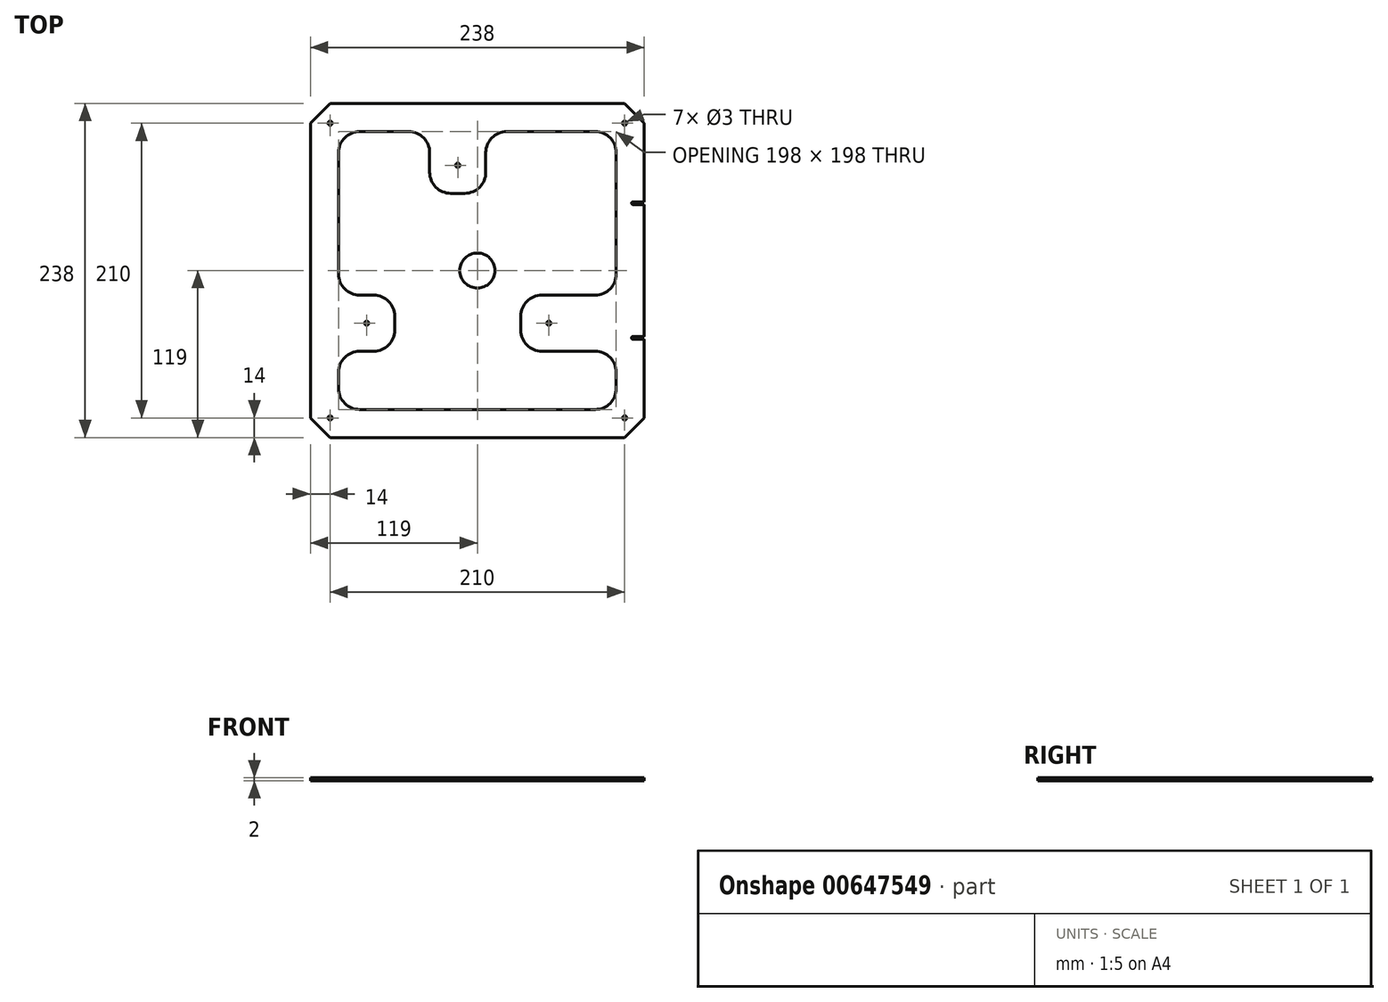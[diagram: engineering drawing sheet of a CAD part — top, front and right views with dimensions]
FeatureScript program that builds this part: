
annotation { "Feature Type Name" : "Feature", "Feature Type Description" : "" }
export const myFeature = defineFeature(function(context is Context, id is Id, definition is map)
    precondition{}
    {
        {
            var Q0;
            Q0=qCreatedBy(makeId("Top.planeOp"),FACE);
            var sketch = newSketch(context, id + "F0", { "sketchPlane" : qUnion([Q0])});
            skLineSegment(sketch, "E0.bottom", {"start": v(105, 119) * mm, "end": v(-105, 119) * mm});
            skLineSegment(sketch, "E0.top", {"start": v(105, -119) * mm, "end": v(-105, -119) * mm});
            skLineSegment(sketch, "E0.left", {"start": v(119, 105) * mm, "end": v(119, -105) * mm});
            skLineSegment(sketch, "E0.right", {"start": v(-119, 105) * mm, "end": v(-119, -105) * mm});
            skPoint(sketch, "E0.middle", {"position": v(0, 0) * mm});
            skLineSegment(sketch, "E1.bottom", {"start": v(105, 105) * mm, "end": v(-105, 105) * mm, "construction": true});
            skLineSegment(sketch, "E1.top", {"start": v(105, -105) * mm, "end": v(-105, -105) * mm, "construction": true});
            skLineSegment(sketch, "E1.left", {"start": v(105, 105) * mm, "end": v(105, -105) * mm, "construction": true});
            skLineSegment(sketch, "E1.right", {"start": v(-105, 105) * mm, "end": v(-105, -105) * mm, "construction": true});
            skPoint(sketch, "E2", {"position": v(-105, 105) * mm});
            skPoint(sketch, "E3", {"position": v(105, 105) * mm});
            skPoint(sketch, "E4", {"position": v(105, -105) * mm});
            skPoint(sketch, "E5", {"position": v(-105, -105) * mm});
            skLineSegment(sketch, "E6", {"start": v(-119, 105) * mm, "end": v(-105, 119) * mm});
            skPoint(sketch, "E7.orphan", {"position": v(-119, 119) * mm});
            skLineSegment(sketch, "E8", {"start": v(105, 119) * mm, "end": v(119, 105) * mm});
            skPoint(sketch, "E9.orphan", {"position": v(119, 119) * mm});
            skLineSegment(sketch, "E10", {"start": v(-119, -105) * mm, "end": v(-105, -119) * mm});
            skPoint(sketch, "E11.orphan", {"position": v(-119, -119) * mm});
            skLineSegment(sketch, "E12", {"start": v(105, -119) * mm, "end": v(119, -105) * mm});
            skPoint(sketch, "E13.orphan", {"position": v(119, -119) * mm});
            skLineSegment(sketch, "E14", {"start": v(-14, 119) * mm, "end": v(-14, -119) * mm, "construction": true});
            skCircle(sketch, "E15", {"center": v(-14, 0) * mm, "radius": 75 * mm, "construction": true});
            skPoint(sketch, "E16", {"position": v(-14, 75) * mm});
            skLineSegment(sketch, "E17", {"start": v(-119, 0) * mm, "end": v(119, 0) * mm, "construction": true});
            skPoint(sketch, "E18.1.0", {"position": v(-78.95, -37.5) * mm});
            skPoint(sketch, "E18.2.0", {"position": v(50.95, -37.5) * mm});
            skSolve(sketch);
        }
        {
            var Q0;
            Q0=makeQuery(id+"F0.imprint","IMPRINT",FACE,{"disambiguationData":[TD([[makeQuery(id+"F0.imprint","IMPRINT",EDGE,{"derivedFrom":sQuery(id+"F0.wireOp",EDGE,"E0.bottom")}),1.0]])]});
            extrude(context, id + "F1", {"entities" : qUnion([Q0]), "depth" : 2 * mm, "offsetDistance" : 25 * mm});
        }
        {
            var Q0;
            Q0=sQuery(id+"F0.wireOp",VERTEX,"E2");
            var Q1;
            Q1=sQuery(id+"F0.wireOp",VERTEX,"E3");
            var Q2;
            Q2=sQuery(id+"F0.wireOp",VERTEX,"E5");
            var Q3;
            Q3=sQuery(id+"F0.wireOp",VERTEX,"E4");
            var Q4;
            Q4=sQuery(id+"F0.wireOp",VERTEX,"E16");
            var Q5;
            Q5=sQuery(id+"F0.wireOp",VERTEX,"E18.2.0");
            var Q6;
            Q6=sQuery(id+"F0.wireOp",VERTEX,"E18.1.0");
            var Q7;
            Q7=makeQuery(id+"F1.opExtrude","SWEPT_BODY",BODY,{"disambiguationData":[OSD([sQuery(id+"F0.wireOp",EDGE,"E0.bottom"),sQuery(id+"F0.wireOp",EDGE,"E0.top"),sQuery(id+"F0.wireOp",EDGE,"E0.left"),sQuery(id+"F0.wireOp",EDGE,"E0.right"),sQuery(id+"F0.wireOp",EDGE,"E6"),sQuery(id+"F0.wireOp",EDGE,"E8"),sQuery(id+"F0.wireOp",EDGE,"E10"),sQuery(id+"F0.wireOp",EDGE,"E12")])]});
            hole(context, id + "F2", {"style" : HoleStyle.SIMPLE, "endStyle" : HoleEndStyle.THROUGH, "oppositeDirection" : true, "holeDiameter" : 3 * mm, "majorDiameter" : 5 * mm, "isTappedThrough" : true, "tappedDepth" : 12 * mm, "tapClearance" : 3, "startFromSketch" : true, "locations" : qUnion([Q0, Q1, Q2, Q3, Q4, Q5, Q6]), "scope" : qUnion([Q7])});
        }
        {
            var Q0;
            Q0=makeQuery(id+"F1.opExtrude","CAP_FACE",FACE,{"disambiguationData":[OSD([sQuery(id+"F0.wireOp",EDGE,"E0.bottom"),sQuery(id+"F0.wireOp",EDGE,"E0.top"),sQuery(id+"F0.wireOp",EDGE,"E0.left"),sQuery(id+"F0.wireOp",EDGE,"E0.right"),sQuery(id+"F0.wireOp",EDGE,"E6"),sQuery(id+"F0.wireOp",EDGE,"E8"),sQuery(id+"F0.wireOp",EDGE,"E10"),sQuery(id+"F0.wireOp",EDGE,"E12")])],"isStart":false});
            var sketch = newSketch(context, id + "F3", { "sketchPlane" : qUnion([Q0])});
            skLineSegment(sketch, "E19", {"start": v(-99, -2.5) * mm, "end": v(-99, 84) * mm});
            skLineSegment(sketch, "E20", {"start": v(21, 99) * mm, "end": v(84, 99) * mm});
            skLineSegment(sketch, "E21", {"start": v(99, 84) * mm, "end": v(99, 40.75) * mm});
            skLineSegment(sketch, "E22", {"start": v(84, -99) * mm, "end": v(-84, -99) * mm});
            skPoint(sketch, "E23.visualSharp", {"position": v(-99, 99) * mm});
            skArc(sketch, "E23.filletArc", {"start": v(-84, 99) * mm, "mid": v(-94.6, 94.6) * mm, "end": v(-99, 84) * mm});
            skPoint(sketch, "E24.visualSharp", {"position": v(99, 99) * mm});
            skArc(sketch, "E24.filletArc", {"start": v(99, 84) * mm, "mid": v(94.6, 94.6) * mm, "end": v(84, 99) * mm});
            skPoint(sketch, "E25.visualSharp", {"position": v(99, -99) * mm});
            skArc(sketch, "E25.filletArc", {"start": v(84, -99) * mm, "mid": v(94.6, -94.6) * mm, "end": v(99, -84) * mm});
            skPoint(sketch, "E26.visualSharp", {"position": v(-99, -99) * mm});
            skArc(sketch, "E26.filletArc", {"start": v(-99, -84) * mm, "mid": v(-94.6, -94.6) * mm, "end": v(-84, -99) * mm});
            skLineSegment(sketch, "E27", {"start": v(-78.95, -37.5) * mm, "end": v(-99, -37.5) * mm, "construction": true});
            skLineSegment(sketch, "E28", {"start": v(-78.95, -37.5) * mm, "end": v(-58.95, -37.5) * mm, "construction": true});
            skLineSegment(sketch, "E29", {"start": v(-58.95, -32.5) * mm, "end": v(-58.95, -42.5) * mm});
            skLineSegment(sketch, "E30", {"start": v(-73.95, -17.5) * mm, "end": v(-84, -17.5) * mm});
            skArc(sketch, "E31.filletArc", {"start": v(-99, -2.5) * mm, "mid": v(-94.6, -13.1) * mm, "end": v(-84, -17.5) * mm});
            skPoint(sketch, "E32.visualSharp", {"position": v(-58.95, -17.5) * mm});
            skArc(sketch, "E32.filletArc", {"start": v(-58.95, -32.5) * mm, "mid": v(-63.35, -21.9) * mm, "end": v(-73.95, -17.5) * mm});
            skLineSegment(sketch, "E33", {"start": v(-73.95, -57.5) * mm, "end": v(-84, -57.5) * mm});
            skPoint(sketch, "E34.visualSharp", {"position": v(-58.95, -57.5) * mm});
            skArc(sketch, "E34.filletArc", {"start": v(-73.95, -57.5) * mm, "mid": v(-63.35, -53.1) * mm, "end": v(-58.95, -42.5) * mm});
            skLineSegment(sketch, "E35", {"start": v(-99, -72.5) * mm, "end": v(-99, -84) * mm});
            skPoint(sketch, "E36.visualSharp", {"position": v(-99, -57.5) * mm});
            skArc(sketch, "E36.filletArc", {"start": v(-84, -57.5) * mm, "mid": v(-94.6, -61.9) * mm, "end": v(-99, -72.5) * mm});
            skLineSegment(sketch, "E37", {"start": v(-14, 55) * mm, "end": v(-14, 99) * mm, "construction": true});
            skPoint(sketch, "E37.endSnap0", {"position": v(0, 99) * mm});
            skPoint(sketch, "E38.orphan", {"position": v(-14, 75) * mm});
            skLineSegment(sketch, "E39", {"start": v(-19, 55) * mm, "end": v(-9, 55) * mm});
            skLineSegment(sketch, "E40", {"start": v(-34, 70) * mm, "end": v(-34, 84) * mm});
            skLineSegment(sketch, "E41", {"start": v(6, 70) * mm, "end": v(6, 84) * mm});
            skArc(sketch, "E42.filletArc", {"start": v(21, 99) * mm, "mid": v(10.4, 94.6) * mm, "end": v(6, 84) * mm});
            skLineSegment(sketch, "E43", {"start": v(-49, 99) * mm, "end": v(-84, 99) * mm});
            skPoint(sketch, "E44.visualSharp", {"position": v(-34, 99) * mm});
            skArc(sketch, "E44.filletArc", {"start": v(-34, 84) * mm, "mid": v(-38.4, 94.6) * mm, "end": v(-49, 99) * mm});
            skPoint(sketch, "E45.visualSharp", {"position": v(-34, 55) * mm});
            skArc(sketch, "E45.filletArc", {"start": v(-34, 70) * mm, "mid": v(-29.6, 59.4) * mm, "end": v(-19, 55) * mm});
            skPoint(sketch, "E46.visualSharp", {"position": v(6, 55) * mm});
            skArc(sketch, "E46.filletArc", {"start": v(-9, 55) * mm, "mid": v(1.6, 59.4) * mm, "end": v(6, 70) * mm});
            skLineSegment(sketch, "E47", {"start": v(30.95, -37.5) * mm, "end": v(99, -37.5) * mm, "construction": true});
            skPoint(sketch, "E48.orphan", {"position": v(50.95, -37.5) * mm});
            skLineSegment(sketch, "E49", {"start": v(30.95, -37.5) * mm, "end": v(30.95, -32.5) * mm});
            skLineSegment(sketch, "E50", {"start": v(45.95, -17.5) * mm, "end": v(84, -17.5) * mm});
            skLineSegment(sketch, "E51", {"start": v(30.95, -37.5) * mm, "end": v(30.95, -42.5) * mm});
            skLineSegment(sketch, "E52", {"start": v(45.95, -57.5) * mm, "end": v(84, -57.5) * mm});
            skArc(sketch, "E53.filletArc", {"start": v(84, -17.5) * mm, "mid": v(94.6, -13.1) * mm, "end": v(99, -2.5) * mm});
            skLineSegment(sketch, "E54", {"start": v(99, -72.5) * mm, "end": v(99, -84) * mm});
            skPoint(sketch, "E55.visualSharp", {"position": v(30.95, -17.5) * mm});
            skArc(sketch, "E55.filletArc", {"start": v(45.95, -17.5) * mm, "mid": v(35.35, -21.9) * mm, "end": v(30.95, -32.5) * mm});
            skPoint(sketch, "E56.visualSharp", {"position": v(30.95, -57.5) * mm});
            skArc(sketch, "E56.filletArc", {"start": v(30.95, -42.5) * mm, "mid": v(35.35, -53.1) * mm, "end": v(45.95, -57.5) * mm});
            skPoint(sketch, "E57.visualSharp", {"position": v(99, -57.5) * mm});
            skArc(sketch, "E57.filletArc", {"start": v(99, -72.5) * mm, "mid": v(94.6, -61.9) * mm, "end": v(84, -57.5) * mm});
            skCircle(sketch, "E58", {"center": v(0, 0) * mm, "radius": 12.5 * mm});
            skLineSegment(sketch, "E59", {"start": v(-119, 0) * mm, "end": v(119, 0) * mm, "construction": true});
            skLineSegment(sketch, "E60", {"start": v(127.52, 47.1) * mm, "end": v(127.52, -47.1) * mm, "construction": true});
            skPoint(sketch, "E61", {"position": v(127.52, 0) * mm});
            skPoint(sketch, "E62.startSnap0", {"position": v(99, 40.75) * mm});
            skLineSegment(sketch, "E63.trimOffspring", {"start": v(99, 40.75) * mm, "end": v(99, -2.5) * mm});
            skLineSegment(sketch, "E64.bottom", {"start": v(119, -47.1) * mm, "end": v(110, -47.1) * mm});
            skLineSegment(sketch, "E64.top", {"start": v(119, -48.9) * mm, "end": v(110, -48.9) * mm});
            skLineSegment(sketch, "E64.left", {"start": v(119, -47.1) * mm, "end": v(119, -48.9) * mm});
            skLineSegment(sketch, "E64.right", {"start": v(110, -47.1) * mm, "end": v(110, -48.9) * mm});
            skLineSegment(sketch, "E65.bottom", {"start": v(119, 48.9) * mm, "end": v(110, 48.9) * mm});
            skLineSegment(sketch, "E65.top", {"start": v(119, 47.1) * mm, "end": v(110, 47.1) * mm});
            skLineSegment(sketch, "E65.left", {"start": v(119, 48.9) * mm, "end": v(119, 47.1) * mm});
            skLineSegment(sketch, "E65.right", {"start": v(110, 48.9) * mm, "end": v(110, 47.1) * mm});
            skSolve(sketch);
        }
        {
            var Q0;
            Q0=makeQuery(id+"F3.imprint","IMPRINT",FACE,{"disambiguationData":[TD([[makeQuery(id+"F3.imprint","IMPRINT",EDGE,{"derivedFrom":sQuery(id+"F3.wireOp",EDGE,"E19")}),-1.0]])]});
            var Q1;
            Q1=makeQuery(id+"F3.imprint","IMPRINT",FACE,{"disambiguationData":[TD([[makeQuery(id+"F3.imprint","IMPRINT",EDGE,{"derivedFrom":sQuery(id+"F3.wireOp",EDGE,"E65.bottom")}),1.0]])]});
            var Q2;
            Q2=makeQuery(id+"F3.imprint","IMPRINT",FACE,{"disambiguationData":[TD([[makeQuery(id+"F3.imprint","IMPRINT",EDGE,{"derivedFrom":sQuery(id+"F3.wireOp",EDGE,"E64.bottom")}),1.0]])]});
            extrude(context, id + "F4", {"entities" : qUnion([Q0, Q1, Q2]), "operationType" : NewBodyOperationType.REMOVE, "oppositeDirection" : true, "depth" : 25 * mm, "offsetDistance" : 25 * mm});
        }
        {
            var Q0;
            Q0=makeQuery(id+"F4.boolean.opBoolean","COPY",EDGE,{"derivedFrom":makeQuery(id+"F4.opExtrude","SWEPT_EDGE",EDGE,{"disambiguationData":[OSD([sQuery(id+"F0.wireOp",EDGE,"E0.left"),sQuery(id+"F3.wireOp",EDGE,"E64.top"),sQuery(id+"F3.wireOp",EDGE,"E64.left")])]})});
            var Q1;
            Q1=makeQuery(id+"F4.boolean.opBoolean","COPY",EDGE,{"derivedFrom":makeQuery(id+"F4.opExtrude","SWEPT_EDGE",EDGE,{"disambiguationData":[OSD([sQuery(id+"F0.wireOp",EDGE,"E0.left"),sQuery(id+"F3.wireOp",EDGE,"E64.bottom"),sQuery(id+"F3.wireOp",EDGE,"E64.left")])]})});
            var Q2;
            Q2=makeQuery(id+"F4.boolean.opBoolean","COPY",EDGE,{"derivedFrom":makeQuery(id+"F4.opExtrude","SWEPT_EDGE",EDGE,{"disambiguationData":[OSD([sQuery(id+"F0.wireOp",EDGE,"E0.left"),sQuery(id+"F3.wireOp",EDGE,"E65.bottom"),sQuery(id+"F3.wireOp",EDGE,"E65.left")])]})});
            var Q3;
            Q3=makeQuery(id+"F4.boolean.opBoolean","COPY",EDGE,{"derivedFrom":makeQuery(id+"F4.opExtrude","SWEPT_EDGE",EDGE,{"disambiguationData":[OSD([sQuery(id+"F0.wireOp",EDGE,"E0.left"),sQuery(id+"F3.wireOp",EDGE,"E65.top"),sQuery(id+"F3.wireOp",EDGE,"E65.left")])]})});
            var Q4;
            Q4=makeQuery(id+"F4.boolean.opBoolean","COPY",EDGE,{"derivedFrom":makeQuery(id+"F4.opExtrude","SWEPT_EDGE",EDGE,{"disambiguationData":[OSD([sQuery(id+"F3.wireOp",EDGE,"E65.bottom"),sQuery(id+"F3.wireOp",EDGE,"E65.right")])]})});
            var Q5;
            Q5=makeQuery(id+"F4.boolean.opBoolean","COPY",EDGE,{"derivedFrom":makeQuery(id+"F4.opExtrude","SWEPT_EDGE",EDGE,{"disambiguationData":[OSD([sQuery(id+"F3.wireOp",EDGE,"E65.top"),sQuery(id+"F3.wireOp",EDGE,"E65.right")])]})});
            var Q6;
            Q6=makeQuery(id+"F4.boolean.opBoolean","COPY",EDGE,{"derivedFrom":makeQuery(id+"F4.opExtrude","SWEPT_EDGE",EDGE,{"disambiguationData":[OSD([sQuery(id+"F3.wireOp",EDGE,"E64.top"),sQuery(id+"F3.wireOp",EDGE,"E64.right")])]})});
            var Q7;
            Q7=makeQuery(id+"F4.boolean.opBoolean","COPY",EDGE,{"derivedFrom":makeQuery(id+"F4.opExtrude","SWEPT_EDGE",EDGE,{"disambiguationData":[OSD([sQuery(id+"F3.wireOp",EDGE,"E64.bottom"),sQuery(id+"F3.wireOp",EDGE,"E64.right")])]})});
            fillet(context, id + "F5", {"entities" : qUnion([Q0, Q1, Q2, Q3, Q4, Q5, Q6, Q7]), "radius" : .75 * mm, "tangentPropagation" : true, "defaultsChanged" : false, "vertexSettings" : [], "allowEdgeOverflow" : false});
        }
    });
